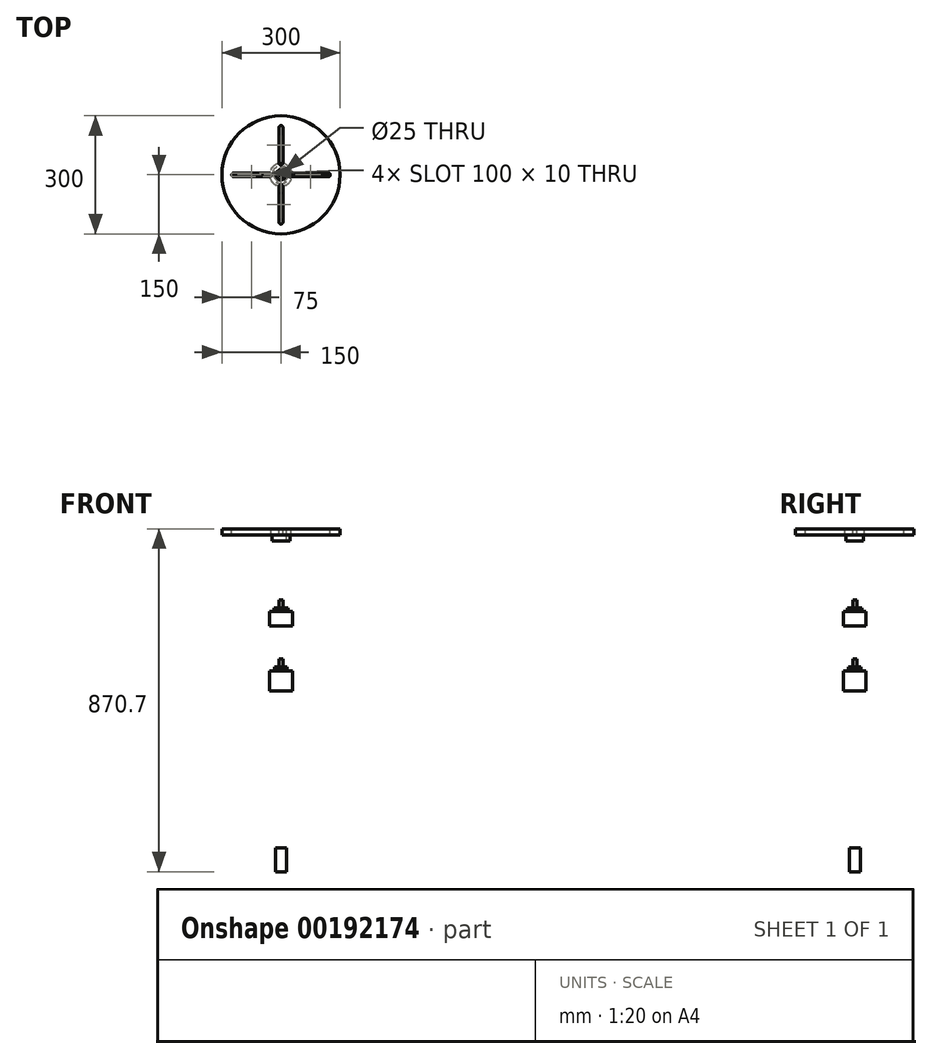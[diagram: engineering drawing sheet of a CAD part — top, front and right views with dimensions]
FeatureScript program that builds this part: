
annotation { "Feature Type Name" : "Feature", "Feature Type Description" : "" }
export const myFeature = defineFeature(function(context is Context, id is Id, definition is map)
    precondition{}
    {
        {
            var Q0;
            Q0=qCreatedBy(makeId("Top.planeOp"),FACE);
            var sketch = newSketch(context, id + "F0", { "sketchPlane" : qUnion([Q0])});
            skCircle(sketch, "E0", {"center": v(0, 0) * mm, "radius": 150 * mm});
            skCircle(sketch, "E1", {"center": v(0, 0) * mm, "radius": 12.5 * mm});
            skSolve(sketch);
        }
        {
            var Q0;
            Q0 = qSketchRegion(id + "F0", true);
            extrude(context, id + "F1", {"entities" : qUnion([Q0]), "depth" : 15 * mm});
        }
        {
            var Q0;
            Q0=makeQuery(id+"F1.opExtrude","CAP_FACE",FACE,{"disambiguationData":[OSD([sQuery(id+"F0.wireOp",EDGE,"E0")])],"isStart":true});
            var sketch = newSketch(context, id + "F2", { "sketchPlane" : qUnion([Q0])});
            skCircle(sketch, "E2", {"center": v(0, 0) * mm, "radius": 22.5 * mm});
            skCircle(sketch, "E3", {"center": v(0, 0) * mm, "radius": 12.5 * mm});
            skSolve(sketch);
        }
        {
            var Q0;
            Q0 = qSketchRegion(id + "F2", true);
            extrude(context, id + "F3", {"entities" : qUnion([Q0]), "operationType" : NewBodyOperationType.ADD, "depth" : 15 * mm});
        }
        {
            var Q0;
            Q0=makeQuery(id+"F1.opExtrude","CAP_FACE",FACE,{"disambiguationData":[OSD([sQuery(id+"F0.wireOp",EDGE,"E0"),sQuery(id+"F0.wireOp",EDGE,"E1")])],"isStart":false});
            var sketch = newSketch(context, id + "F4", { "sketchPlane" : qUnion([Q0])});
            skLineSegment(sketch, "E4", {"start": v(0, 0) * mm, "end": v(150, 0) * mm, "construction": true});
            skLineSegment(sketch, "E5", {"start": v(0, 0) * mm, "end": v(0, -150) * mm, "construction": true});
            skLineSegment(sketch, "E6", {"start": v(0, -150) * mm, "end": v(0, -120) * mm, "construction": true});
            skLineSegment(sketch, "E7", {"start": v(0, 0) * mm, "end": v(0, -30) * mm, "construction": true});
            skLineSegment(sketch, "E8", {"start": v(0, -30) * mm, "end": v(0, -120) * mm});
            skLineSegment(sketch, "E9.0", {"start": v(-5, -30) * mm, "end": v(-5, -120) * mm});
            skLineSegment(sketch, "E10.MirrorCS", {"start": v(5, -30) * mm, "end": v(5, -120) * mm});
            skLineSegment(sketch, "E11", {"start": v(0, -30) * mm, "end": v(0, -25) * mm});
            skArc(sketch, "E12", {"start": v(5, -30) * mm, "mid": v(0, -25) * mm, "end": v(-5, -30) * mm});
            skArc(sketch, "E13", {"start": v(-5, -120) * mm, "mid": v(0, -125) * mm, "end": v(5, -120) * mm});
            skLineSegment(sketch, "E14.1.0", {"start": v(30, 5) * mm, "end": v(120, 5) * mm});
            skLineSegment(sketch, "E14.1.1", {"start": v(30, -5) * mm, "end": v(120, -5) * mm});
            skArc(sketch, "E14.1.2", {"start": v(30, 5) * mm, "mid": v(25, 0) * mm, "end": v(30, -5) * mm});
            skArc(sketch, "E14.1.3", {"start": v(120, -5) * mm, "mid": v(125, 0) * mm, "end": v(120, 5) * mm});
            skLineSegment(sketch, "E14.2.0", {"start": v(-5, 30) * mm, "end": v(-5, 120) * mm});
            skLineSegment(sketch, "E14.2.1", {"start": v(5, 30) * mm, "end": v(5, 120) * mm});
            skArc(sketch, "E14.2.2", {"start": v(-5, 30) * mm, "mid": v(0, 25) * mm, "end": v(5, 30) * mm});
            skArc(sketch, "E14.2.3", {"start": v(5, 120) * mm, "mid": v(0, 125) * mm, "end": v(-5, 120) * mm});
            skLineSegment(sketch, "E14.3.0", {"start": v(-30, -5) * mm, "end": v(-120, -5) * mm});
            skLineSegment(sketch, "E14.3.1", {"start": v(-30, 5) * mm, "end": v(-120, 5) * mm});
            skArc(sketch, "E14.3.2", {"start": v(-30, -5) * mm, "mid": v(-25, 0) * mm, "end": v(-30, 5) * mm});
            skArc(sketch, "E14.3.3", {"start": v(-120, 5) * mm, "mid": v(-125, 0) * mm, "end": v(-120, -5) * mm});
            skPoint(sketch, "E14.center", {"position": v(0, 0) * mm});
            skSolve(sketch);
        }
        {
            var Q0;
            Q0 = qSketchRegion(id + "F4", true);
            extrude(context, id + "F5", {"entities" : qUnion([Q0]), "operationType" : NewBodyOperationType.REMOVE, "oppositeDirection" : true, "depth" : 25 * mm});
        }
        {
            var Q0;
            Q0=makeQuery(id+"F3.opExtrude","CAP_FACE",FACE,{"disambiguationData":[OSD([sQuery(id+"F2.wireOp",EDGE,"E2"),sQuery(id+"F2.wireOp",EDGE,"E3")])],"isStart":false});
            cPlane(context, id + "F6", {"entities" : qUnion([Q0]), "cplaneType" : CPlaneType.OFFSET, "offset" : 150 * mm, "width" : 150 * mm, "height" : 150 * mm});
        }
        {
            var Q0;
            Q0=qCreatedBy(id+"F6.planeOp",FACE);
            var sketch = newSketch(context, id + "F7", { "sketchPlane" : qUnion([Q0])});
            skCircle(sketch, "E15", {"center": v(0, 0) * mm, "radius": 5 * mm});
            skSolve(sketch);
        }
        {
            var Q0;
            Q0 = qSketchRegion(id + "F7", true);
            extrude(context, id + "F8", {"entities" : qUnion([Q0]), "depth" : 20 * mm});
        }
        {
            var Q0;
            Q0=makeQuery(id+"F8.opExtrude","CAP_FACE",FACE,{"disambiguationData":[OSD([sQuery(id+"F7.wireOp",EDGE,"E15")])],"isStart":false});
            var sketch = newSketch(context, id + "F9", { "sketchPlane" : qUnion([Q0])});
            skCircle(sketch, "E16", {"center": v(0, 0) * mm, "radius": 17.95 * mm});
            skSolve(sketch);
        }
        {
            var Q0;
            Q0 = qSketchRegion(id + "F9", true);
            extrude(context, id + "F10", {"entities" : qUnion([Q0]), "operationType" : NewBodyOperationType.ADD, "depth" : 9.8 * mm});
        }
        {
            var Q0;
            Q0=makeQuery(id+"F10.opExtrude","CAP_FACE",FACE,{"disambiguationData":[OSD([sQuery(id+"F9.wireOp",EDGE,"E16")])],"isStart":false});
            var sketch = newSketch(context, id + "F11", { "sketchPlane" : qUnion([Q0])});
            skCircle(sketch, "E17", {"center": v(0, 0) * mm, "radius": 29 * mm});
            skSolve(sketch);
        }
        {
            var Q0;
            Q0 = qSketchRegion(id + "F11", true);
            extrude(context, id + "F12", {"entities" : qUnion([Q0]), "operationType" : NewBodyOperationType.ADD, "depth" : 36 * mm});
        }
        {
            var Q0;
            Q0=qCreatedBy(id+"F6.planeOp",FACE);
            cPlane(context, id + "F13", {"entities" : qUnion([Q0]), "cplaneType" : CPlaneType.OFFSET, "offset" : 150 * mm, "width" : 150 * mm, "height" : 150 * mm});
        }
        {
            var Q0;
            Q0=qCreatedBy(id+"F13.planeOp",FACE);
            var sketch = newSketch(context, id + "F14", { "sketchPlane" : qUnion([Q0])});
            skCircle(sketch, "E18", {"center": v(0, 0) * mm, "radius": 5 * mm});
            skSolve(sketch);
        }
        {
            var Q0;
            Q0 = qSketchRegion(id + "F14", true);
            extrude(context, id + "F15", {"entities" : qUnion([Q0]), "depth" : 20 * mm});
        }
        {
            var Q0;
            Q0=makeQuery(id+"F15.opExtrude","CAP_FACE",FACE,{"disambiguationData":[OSD([sQuery(id+"F14.wireOp",EDGE,"E18")])],"isStart":false});
            var sketch = newSketch(context, id + "F16", { "sketchPlane" : qUnion([Q0])});
            skCircle(sketch, "E19", {"center": v(0, 0) * mm, "radius": 15.75 * mm});
            skSolve(sketch);
        }
        {
            var Q0;
            Q0 = qSketchRegion(id + "F16", true);
            extrude(context, id + "F17", {"entities" : qUnion([Q0]), "operationType" : NewBodyOperationType.ADD, "depth" : 8 * mm});
        }
        {
            var Q0;
            Q0=makeQuery(id+"F17.opExtrude","CAP_FACE",FACE,{"disambiguationData":[OSD([sQuery(id+"F16.wireOp",EDGE,"E19")])],"isStart":false});
            var sketch = newSketch(context, id + "F18", { "sketchPlane" : qUnion([Q0])});
            skCircle(sketch, "E20", {"center": v(0, 0) * mm, "radius": 17.8 * mm});
            skSolve(sketch);
        }
        {
            var Q0;
            Q0 = qSketchRegion(id + "F18", true);
            extrude(context, id + "F19", {"entities" : qUnion([Q0]), "operationType" : NewBodyOperationType.ADD, "depth" : 2 * mm});
        }
        {
            var Q0;
            Q0=makeQuery(id+"F19.opExtrude","CAP_FACE",FACE,{"disambiguationData":[OSD([sQuery(id+"F18.wireOp",EDGE,"E20")])],"isStart":false});
            var sketch = newSketch(context, id + "F20", { "sketchPlane" : qUnion([Q0])});
            skCircle(sketch, "E21", {"center": v(0, 0) * mm, "radius": 29 * mm});
            skSolve(sketch);
        }
        {
            var Q0;
            Q0 = qSketchRegion(id + "F20", true);
            extrude(context, id + "F21", {"entities" : qUnion([Q0]), "operationType" : NewBodyOperationType.ADD, "depth" : 50.7 * mm});
        }
        {
            var Q0;
            Q0=makeQuery(id+"F21.opExtrude","CAP_FACE",FACE,{"disambiguationData":[OSD([sQuery(id+"F20.wireOp",EDGE,"E21")])],"isStart":false});
            cPlane(context, id + "F22", {"entities" : qUnion([Q0]), "cplaneType" : CPlaneType.OFFSET, "offset" : 400 * mm, "width" : 150 * mm, "height" : 150 * mm});
        }
        {
            var Q0;
            Q0=qCreatedBy(id+"F22.planeOp",FACE);
            var sketch = newSketch(context, id + "F23", { "sketchPlane" : qUnion([Q0])});
            skCircle(sketch, "E22", {"center": v(0, 0) * mm, "radius": 14 * mm});
            skSolve(sketch);
        }
        {
            var Q0;
            Q0 = qSketchRegion(id + "F23", true);
            extrude(context, id + "F24", {"entities" : qUnion([Q0]), "depth" : 60 * mm});
        }
        {
            var Q0;
            Q0=qCreatedBy(makeId("Front.planeOp"),FACE);
            cPlane(context, id + "F25", {"entities" : qUnion([Q0]), "cplaneType" : CPlaneType.OFFSET, "offset" : 112 * mm, "oppositeDirection" : true, "width" : 150 * mm, "height" : 150 * mm});
        }
    });
